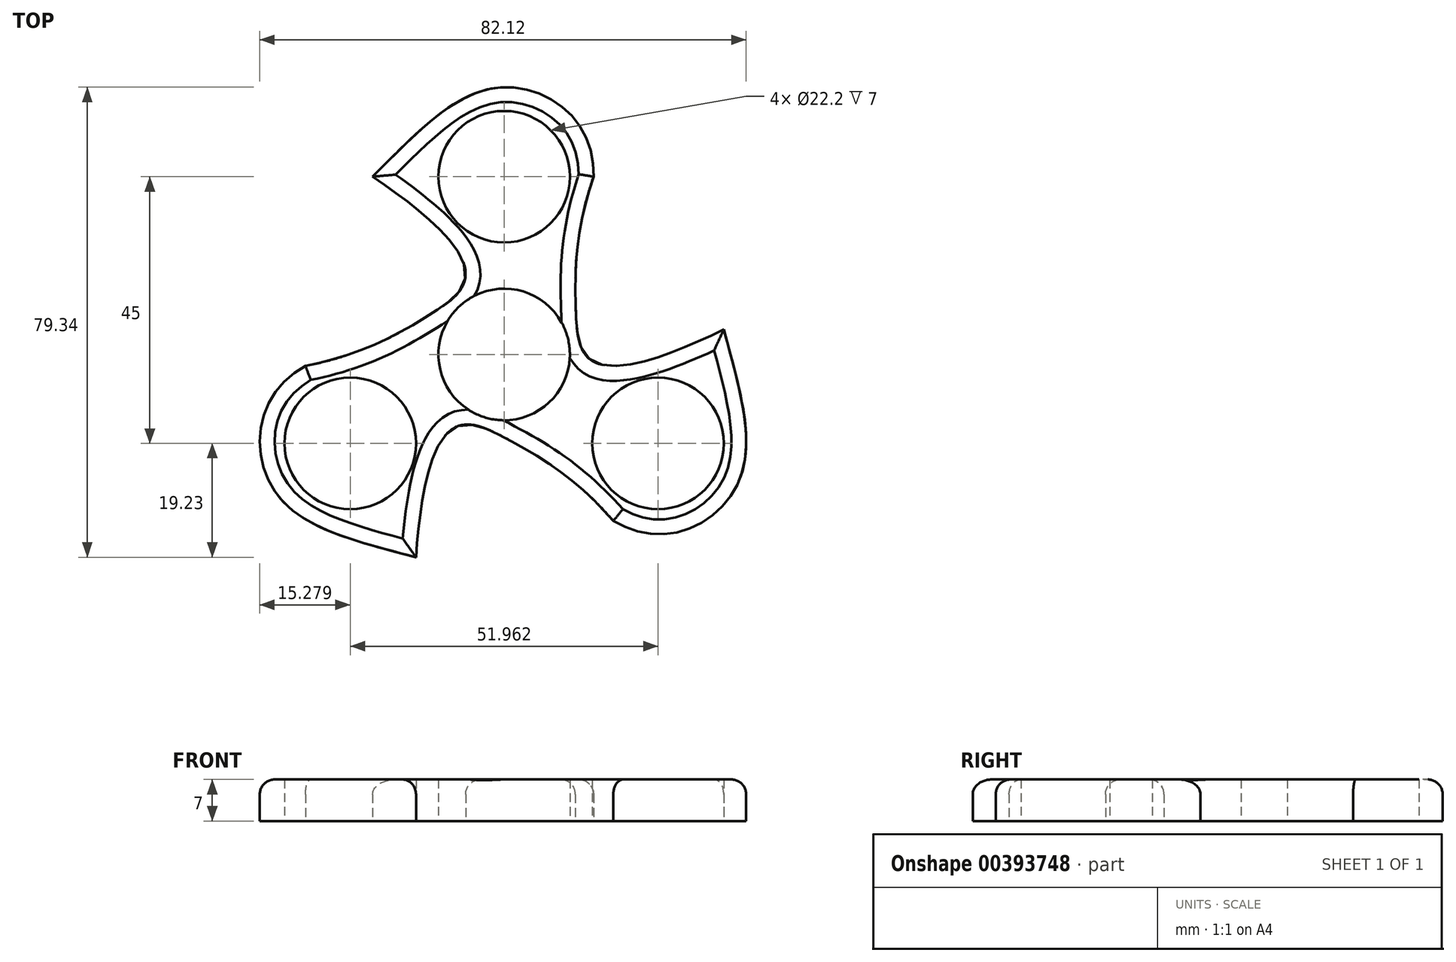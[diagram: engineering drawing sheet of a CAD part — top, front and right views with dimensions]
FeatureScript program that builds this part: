
annotation { "Feature Type Name" : "Feature", "Feature Type Description" : "" }
export const myFeature = defineFeature(function(context is Context, id is Id, definition is map)
    precondition{}
    {
        {
            var Q0;
            Q0=qCreatedBy(makeId("Top.planeOp"),FACE);
            var sketch = newSketch(context, id + "F0", { "sketchPlane" : qUnion([Q0])});
            skCircle(sketch, "E0", {"center": v(0, 0) * mm, "radius": 11.1 * mm});
            skCircle(sketch, "E1", {"center": v(0, 30) * mm, "radius": 11.1 * mm});
            skLineSegment(sketch, "E2", {"start": v(0, 0) * mm, "end": v(0, 30) * mm, "construction": true});
            skLineSegment(sketch, "E3", {"start": v(0, 30) * mm, "end": v(-22.2, 30) * mm, "construction": true});
            skLineSegment(sketch, "E4", {"start": v(0, 30) * mm, "end": v(15.1, 30) * mm, "construction": true});
            skLineSegment(sketch, "E5", {"start": v(0, 30) * mm, "end": v(0, 45.1) * mm, "construction": true});
            skLineSegment(sketch, "E6.1.0", {"start": v(-25.98, -15) * mm, "end": v(-33.53, -1.92) * mm, "construction": true});
            skLineSegment(sketch, "E6.1.1", {"start": v(-25.98, -15) * mm, "end": v(-39.06, -22.55) * mm, "construction": true});
            skLineSegment(sketch, "E6.1.2", {"start": v(-25.98, -15) * mm, "end": v(-14.88, -34.23) * mm, "construction": true});
            skCircle(sketch, "E6.1.3", {"center": v(-25.98, -15) * mm, "radius": 11.1 * mm});
            skLineSegment(sketch, "E6.1.4", {"start": v(0, 0) * mm, "end": v(-25.98, -15) * mm, "construction": true});
            skLineSegment(sketch, "E6.2.0", {"start": v(25.98, -15) * mm, "end": v(18.43, -28.08) * mm, "construction": true});
            skLineSegment(sketch, "E6.2.1", {"start": v(25.98, -15) * mm, "end": v(39.06, -22.55) * mm, "construction": true});
            skLineSegment(sketch, "E6.2.2", {"start": v(25.98, -15) * mm, "end": v(37.08, 4.23) * mm, "construction": true});
            skCircle(sketch, "E6.2.3", {"center": v(25.98, -15) * mm, "radius": 11.1 * mm});
            skLineSegment(sketch, "E6.2.4", {"start": v(0, 0) * mm, "end": v(25.98, -15) * mm, "construction": true});
            skLineSegment(sketch, "E7", {"start": v(0, 0) * mm, "end": v(-12.12, 7) * mm, "construction": true});
            skLineSegment(sketch, "E8.1.0", {"start": v(0, 0) * mm, "end": v(0, -14) * mm, "construction": true});
            skLineSegment(sketch, "E8.2.0", {"start": v(0, 0) * mm, "end": v(12.12, 7) * mm, "construction": true});
            skFitSpline(sketch, "E9", {"points": [v(-22.2, 30) * mm, v(0, 45.1) * mm, v(15.1, 30) * mm], "startDerivative": vector(44.63, 44.58) * mm, "endDerivative": vector(-1.2, -64.1) * mm});
            skFitSpline(sketch, "E10", {"points": [v(37.08, 4.23) * mm, v(39.06, -22.55) * mm, v(18.43, -28.08) * mm], "startDerivative": vector(16.3, -60.94) * mm, "endDerivative": vector(-54.91, 33.08) * mm});
            skFitSpline(sketch, "E11", {"points": [v(-14.88, -34.23) * mm, v(-39.06, -22.55) * mm, v(-33.53, -1.92) * mm], "startDerivative": vector(-60.93, 16.36) * mm, "endDerivative": vector(56.1, 31.02) * mm});
            skFitSpline(sketch, "E12", {"points": [v(15.1, 30) * mm, v(12.12, 7) * mm, v(37.08, 4.23) * mm], "startDerivative": vector(-19.55, -57.1) * mm, "endDerivative": vector(141.73, 68.98) * mm});
            skFitSpline(sketch, "E13", {"points": [v(18.43, -28.08) * mm, v(0, -14) * mm, v(-14.88, -34.23) * mm], "startDerivative": vector(-39.67, 45.48) * mm, "endDerivative": vector(-11.12, -157.23) * mm});
            skFitSpline(sketch, "E14", {"points": [v(-33.53, -1.92) * mm, v(-12.12, 7) * mm, v(-22.2, 30) * mm], "startDerivative": vector(59.23, 11.62) * mm, "endDerivative": vector(-130.6, 88.25) * mm});
            skLineSegment(sketch, "E15", {"start": v(18.43, -28.08) * mm, "end": v(27.06, -33.28) * mm});
            skLineSegment(sketch, "E16.1.0", {"start": v(15.1, 30) * mm, "end": v(15.29, 40.07) * mm});
            skLineSegment(sketch, "E16.2.0", {"start": v(-33.53, -1.92) * mm, "end": v(-42.35, -6.8) * mm});
            skSolve(sketch);
        }
        {
            var Q0;
            Q0=makeQuery(id+"F0.imprint","IMPRINT",FACE,{"disambiguationData":[TD([[makeQuery(id+"F0.imprint","IMPRINT",EDGE,{"derivedFrom":sQuery(id+"F0.wireOp",EDGE,"E0")}),-1.0]])]});
            extrude(context, id + "F1", {"entities" : qUnion([Q0]), "endBound" : BoundingType.SYMMETRIC, "depth" : 7 * mm});
        }
        {
            var Q0;
            Q0=makeQuery(id+"F1.opExtrude","CAP_EDGE",EDGE,{"disambiguationData":[OSD([sQuery(id+"F0.wireOp",EDGE,"E9")])],"isStart":false});
            var Q1;
            Q1=makeQuery(id+"F1.opExtrude","CAP_EDGE",EDGE,{"disambiguationData":[OSD([sQuery(id+"F0.wireOp",EDGE,"E12")])],"isStart":false});
            var Q2;
            Q2=makeQuery(id+"F1.opExtrude","CAP_EDGE",EDGE,{"disambiguationData":[OSD([sQuery(id+"F0.wireOp",EDGE,"E10")])],"isStart":false});
            var Q3;
            Q3=makeQuery(id+"F1.opExtrude","CAP_EDGE",EDGE,{"disambiguationData":[OSD([sQuery(id+"F0.wireOp",EDGE,"E13")])],"isStart":false});
            var Q4;
            Q4=makeQuery(id+"F1.opExtrude","CAP_EDGE",EDGE,{"disambiguationData":[OSD([sQuery(id+"F0.wireOp",EDGE,"E11")])],"isStart":false});
            var Q5;
            Q5=makeQuery(id+"F1.opExtrude","CAP_EDGE",EDGE,{"disambiguationData":[OSD([sQuery(id+"F0.wireOp",EDGE,"E14")])],"isStart":false});
            fillet(context, id + "F2", {"entities" : qUnion([Q0, Q1, Q2, Q3, Q4, Q5]), "radius" : 2.5 * mm, "tangentPropagation" : true, "allowEdgeOverflow" : false});
        }
    });
